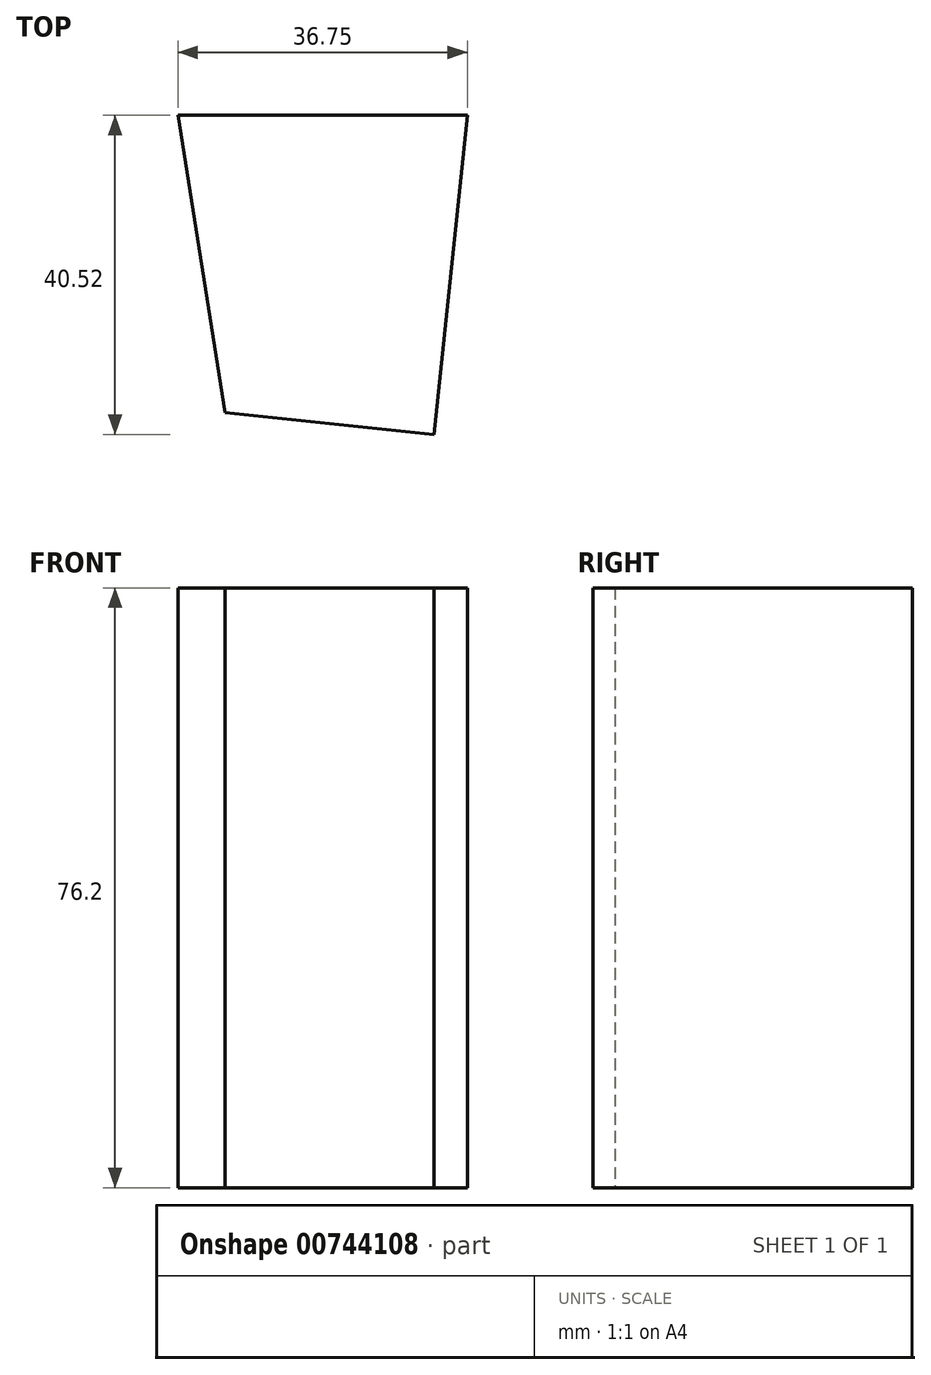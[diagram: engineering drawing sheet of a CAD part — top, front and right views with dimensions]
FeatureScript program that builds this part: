
annotation { "Feature Type Name" : "Feature", "Feature Type Description" : "" }
export const myFeature = defineFeature(function(context is Context, id is Id, definition is map)
    precondition{}
    {
        {
            var Q0;
            Q0=qCreatedBy(makeId("Top.planeOp"),FACE);
            var sketch = newSketch(context, id + "F0", { "sketchPlane" : qUnion([Q0])});
            skLineSegment(sketch, "E0", {"start": v(0, 0) * mm, "end": v(36.75, 0) * mm});
            skLineSegment(sketch, "E1", {"start": v(36.75, 0) * mm, "end": v(32.52, -40.52) * mm});
            skLineSegment(sketch, "E2", {"start": v(32.52, -40.52) * mm, "end": v(5.97, -37.75) * mm});
            skLineSegment(sketch, "E3", {"start": v(5.97, -37.75) * mm, "end": v(0, 0) * mm});
            skSolve(sketch);
        }
        {
            var Q0;
            Q0=makeQuery(id+"F0.imprint","IMPRINT",FACE,{"disambiguationData":[TD([[makeQuery(id+"F0.imprint","IMPRINT",EDGE,{"derivedFrom":sQuery(id+"F0.wireOp",EDGE,"E0")}),-1.0]])]});
            extrude(context, id + "F1", {"entities" : qUnion([Q0]), "depth" : 76.2 * mm, "offsetDistance" : 25.4 * mm});
        }
    });
